# Revit family: 19.Гибкая вставка ANR B1
name_source: partatom
category: Оборудование
revit_build: Autodesk Revit 2016 (Build: 20161004_0715(x64)
units: mm (PartAtom-declared; Revit-internal decimal feet)

## family parameters
Всегда вертикально = Да
На основе рабочей плоскости = Нет
Общий = Нет
При загрузке вырезать с полостями = Нет
Размер круглого соединителя = Использовать диаметр
Тип детали = Нормальный
Точка расчета площади = Нет

## types (8) — shared parameters
Д = 150 мм
Д1 = 130 мм
Единица измерения = шт.
Завод изготовитель = KORF
Ключевая пометка = Вентиляция
Наименование и тех.хар-ка = Гибкая вставка
Раздел = ОВ
№40 = Нет
№45 = Нет

## per-type parameters (varying)
| type | А | А1 | Б | Б1 | Высота | Материал | Р | Середина | Ширина | №12 | №20 | №25 | №30 | №35 | №6 | №7 | №8 |
| ANR 6 B1 | 1022 мм | 992 мм | 1022 мм | 992 мм | 972 мм | резина | 25 мм | 511 мм | 972 мм | Нет | Нет | Нет | Нет | Нет | Да | Нет | Нет |
| ANR 7 B1 | 1022 мм | 992 мм | 1242 мм | 1212 мм | 1181 мм | Сталь серая | 31 мм | 621 мм | 961 мм | Нет | Нет | Нет | Нет | Нет | Нет | Да | Нет |
| ANR 8 B1 | 1242 мм | 1210 мм | 1242 мм | 1212 мм | 1181 мм | Сталь серая | 31 мм | 621 мм | 1181 мм | Нет | Нет | Нет | Нет | Нет | Нет | Нет | Да |
| ANR 12 B1 | 1357 мм | 1328 мм | 1357 мм | 1328 мм | 1290 мм | Сталь серая | 34 мм | 679 мм | 1290 мм | Да | Нет | Нет | Нет | Нет | Нет | Нет | Нет |
| ANR 20 B1 | 1582 мм | 1552 мм | 1582 мм | 1552 мм | 1504 мм | Сталь серая | 39 мм | 791 мм | 1504 мм | Нет | Да | Нет | Нет | Нет | Нет | Нет | Нет |
| ANR 25 B1 | 1968 мм | 1938 мм | 1968 мм | 1938 мм | 1871 мм | Сталь серая | 49 мм | 984 мм | 1871 мм | Нет | Нет | Да | Нет | Нет | Нет | Нет | Нет |
| ANR 30 B1 | 2408 мм | 2381 мм | 1968 мм | 1938 мм | 1871 мм | Сталь серая | 49 мм | 984 мм | 2311 мм | Нет | Нет | Нет | Да | Нет | Нет | Нет | Нет |
| ANR 35 B1 | 2408 мм | 2381 мм | 2408 мм | 2381 мм | 2289 мм | Сталь серая | 59 мм | 1204 мм | 2289 мм | Нет | Нет | Нет | Нет | Да | Нет | Нет | Нет |

note: column(s) folded — value = type name in every type: Тип, марка, обозначение
